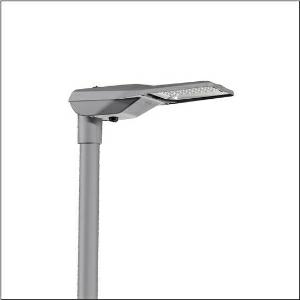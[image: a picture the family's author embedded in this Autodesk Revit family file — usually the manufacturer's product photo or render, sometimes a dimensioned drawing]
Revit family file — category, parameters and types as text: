
# Revit family: streetlight_sl_21_mini___p1_0a_5xe2a43t08hb_b918
name_source: partatom
category: Lighting Fixtures
units: mm (PartAtom-declared; Revit-internal decimal feet)

## family parameters
Cut with Voids When Loaded = No
Host = Face
Light Source = No
Part Type = Normal
Room Calculation Point = No
Round Connector Dimension = Use Diameter
Shared = No

## types (1)
- --- (1 x LED, 9430 lm, 66 W, 4000K)
    Apparent Load = 66 VA
    CIE Flux Codes = 21 50 90 100 100
    Color Rendering = 70
    Color Temperature = 4000K
    Default Elevation = 1800 mm
    Description = Streetlight SL 21 mini, mast luminaire, primary light control with lens, of PMMA, primary optical cover: cover, of toughened safety glass, transparent, light distribution: P1.0a, light emission: direct distribution, primary light characteristic: asymmetric, installation type: side-entry, post-top, LED, High Power LED, rated luminous flux: 9.430lm, luminous efficacy: 143lm/W, light colour: 740, colour temperature: 4000K, control gear: D4i, control: overheat protection, constant luminous flux control, time-dependent luminous flux control, flexible luminous flux parameterisation, pre-setting: logarithmic dimming characteristic, mains connection: 220..240V, AC, 50/60Hz, start of lifetime: 66W, end of service life: 69W, reduction: 30W, luminaire housing, of diecast aluminium, powder-coated, Siteco® metallic grey (DB 702S), corrosivity category C5 mid according to DIN EN ISO 12944, please order mast flange separately, inclination adjustable: 0°, 5°, 10°, 15°, sealing non-destructively replaceable, multi-level sealing system, length: 628mm, width: 235mm, height: 110mm, mast flange for spigot size: 42mm (side-entry): 5XC10008XM4, 60/48mm (side-entry/post-top): 5XC10108XM2, 76/60mm (side-entry/post-top): 5XC10108XM1, mounting height: 4..8m, Smart Interface below and above, protection rating (complete): IP66, insulation class (complete): insulation class II (safety insulation), certification: CE, ENEC, ENEC+, VDE, impact resistance: IK10, permissible operating ambient temperature for outdoor applications: -40..+50°C, standard-compliant lighting for roads and squares, packaging unit: 1 piece

Light Distribution: P1.0a
    Height = 110 mm
    Lamp = 1 x LED
    Lamp Light Flux = 9430 lm
    Lamp Power = 66 W
    Lamp count = 1
    Length = 625 mm
    Luminous efficacy = 143 lm/W
    Manufacturer = Siteco
    ModVariant = No
    Model = 5XE2A43T08HB
    Number of Poles = 1
    OnlyDefault = Yes
    Power Factor = 1
    Product Name = Streetlight SL 21 mini | P1.0a
    Product group = mast luminaire | pylon top
    ProductGroupID = 6100
    Protection Class = Protection class II
    Protection Degree = IP 66
    RLX_Detail_Level = 1
    RLX_Emergency_Light_Flux = 0 lm
    RLX_Emergency_Type = 0
    RLX_Emergency_Type_DB = No
    RlxData = <blob elided: 37541 chars, md5=4ca53174>
    Socket = socket
    Standby Power = 0 W
    System Light Flux = 9430 lm
    System Power = 66 W
    Type Comments = factory setting: luminous flux: 100 % | dim-lin: 254 | 670 mA
    Type Image = l_1003514.jpg
    URL = http://relux.com
    VarID = @adj_186442
    Voltage = 0 V
    Weight = 0.00 kg
    Width = 234 mm

## geometry (parser evidence)
native form markers: Blend x4, Sweep x10
no freeform markers — native parametric forms only
